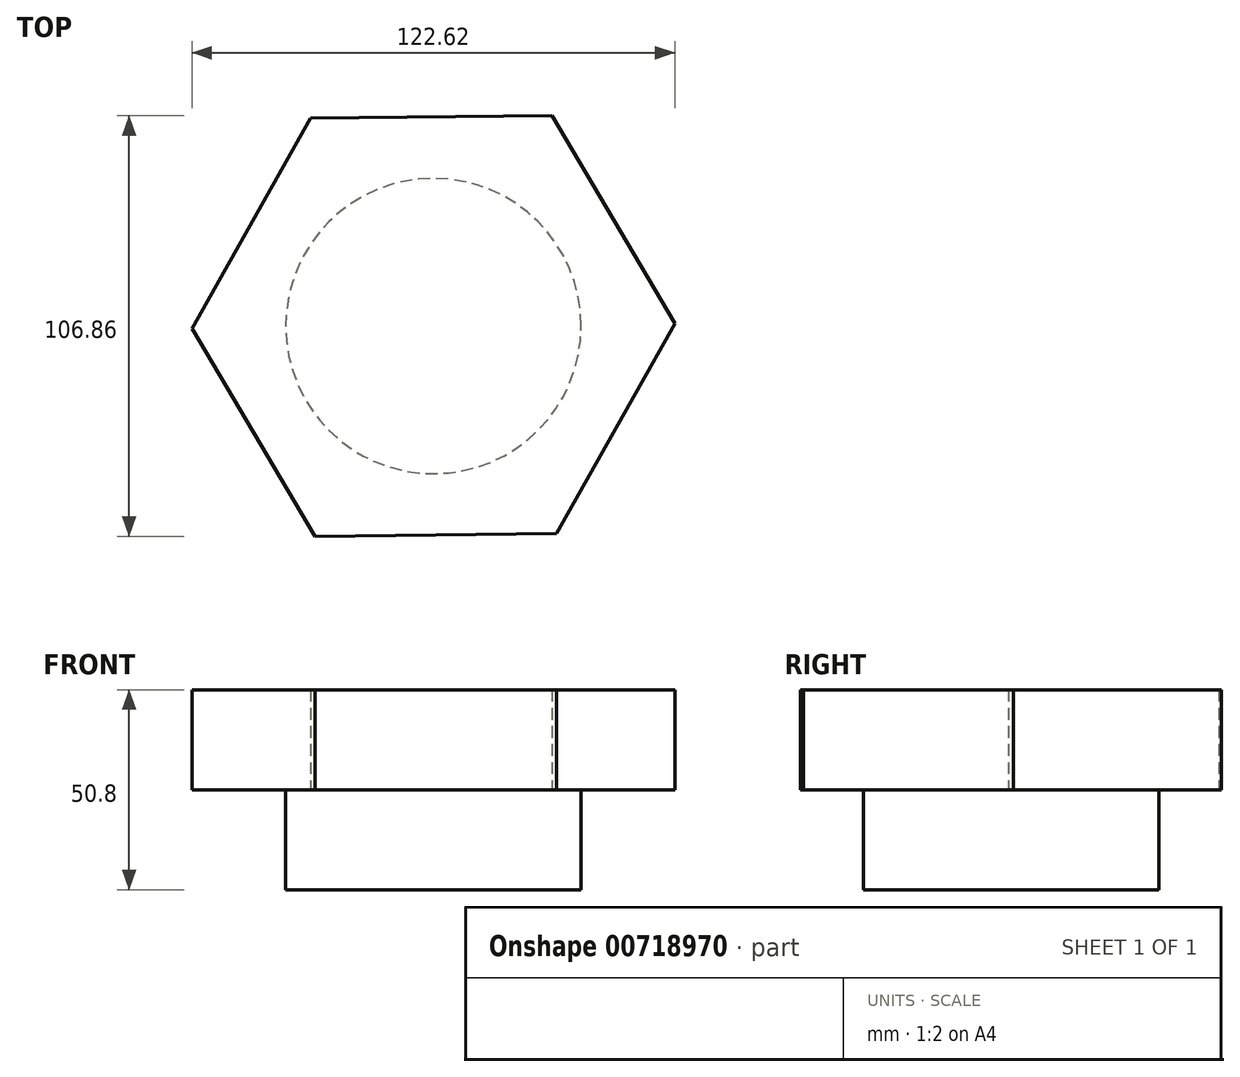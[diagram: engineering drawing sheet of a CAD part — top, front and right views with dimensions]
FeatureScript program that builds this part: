
annotation { "Feature Type Name" : "Feature", "Feature Type Description" : "" }
export const myFeature = defineFeature(function(context is Context, id is Id, definition is map)
    precondition{}
    {
        {
            var Q0;
            Q0=qCreatedBy(makeId("Top.planeOp"),FACE);
            var sketch = newSketch(context, id + "F0", { "sketchPlane" : qUnion([Q0])});
            skCircle(sketch, "E0.cCircle", {"center": v(0, 0) * mm, "radius": 53.1 * mm, "construction": true});
            skLineSegment(sketch, "E0.0", {"start": v(61.31, 0.66) * mm, "end": v(31.23, -52.77) * mm});
            skLineSegment(sketch, "E0.1", {"start": v(31.23, -52.77) * mm, "end": v(-30.08, -53.43) * mm});
            skLineSegment(sketch, "E0.2", {"start": v(-30.08, -53.43) * mm, "end": v(-61.31, -0.66) * mm});
            skLineSegment(sketch, "E0.3", {"start": v(-61.31, -0.66) * mm, "end": v(-31.23, 52.77) * mm});
            skLineSegment(sketch, "E0.4", {"start": v(-31.23, 52.77) * mm, "end": v(30.08, 53.43) * mm});
            skLineSegment(sketch, "E0.5", {"start": v(30.08, 53.43) * mm, "end": v(61.31, 0.66) * mm});
            skPoint(sketch, "E0.0.midPoint", {"position": v(46.27, -26.05) * mm});
            skSolve(sketch);
        }
        {
            var Q0;
            Q0 = qSketchRegion(id + "F0", true);
            var Q1;
            Q1=makeQuery(id+"F0.imprint","IMPRINT",FACE,{"disambiguationData":[TD([[makeQuery(id+"F0.imprint","IMPRINT",EDGE,{"derivedFrom":sQuery(id+"F0.wireOp",EDGE,"E0.0")}),-1.0]])]});
            extrude(context, id + "F1", {"entities" : qUnion([Q0, Q1]), "depth" : 25.4 * mm, "offsetDistance" : 25.4 * mm});
        }
        {
            var Q0;
            Q0=makeQuery(id+"F1.opExtrude","CAP_FACE",FACE,{"disambiguationData":[OSD([sQuery(id+"F0.wireOp",EDGE,"E0.0"),sQuery(id+"F0.wireOp",EDGE,"E0.1"),sQuery(id+"F0.wireOp",EDGE,"E0.2"),sQuery(id+"F0.wireOp",EDGE,"E0.3"),sQuery(id+"F0.wireOp",EDGE,"E0.4"),sQuery(id+"F0.wireOp",EDGE,"E0.5")])],"isStart":true});
            var sketch = newSketch(context, id + "F2", { "sketchPlane" : qUnion([Q0])});
            skCircle(sketch, "E1", {"center": v(0, 0) * mm, "radius": 37.52 * mm});
            skSolve(sketch);
        }
        {
            var Q0;
            Q0=makeQuery(id+"F2.imprint","IMPRINT",FACE,{"disambiguationData":[TD([[makeQuery(id+"F2.imprint","IMPRINT",EDGE,{"derivedFrom":sQuery(id+"F2.wireOp",EDGE,"E1")}),1.0]])]});
            var sketch = newSketch(context, id + "F3", { "sketchPlane" : qUnion([Q0])});
            skSolve(sketch);
        }
        {
            var Q0;
            Q0=makeQuery(id+"F3.imprint","IMPRINT",FACE,{"disambiguationData":[TD([[makeQuery(id+"F3.imprint","IMPRINT",EDGE,{"derivedFrom":makeQuery(id+"F2.imprint","IMPRINT",EDGE,{"derivedFrom":sQuery(id+"F2.wireOp",EDGE,"E1")})}),1.0]])]});
            extrude(context, id + "F4", {"entities" : qUnion([Q0]), "depth" : 25.4 * mm, "offsetDistance" : 25.4 * mm});
        }
    });
